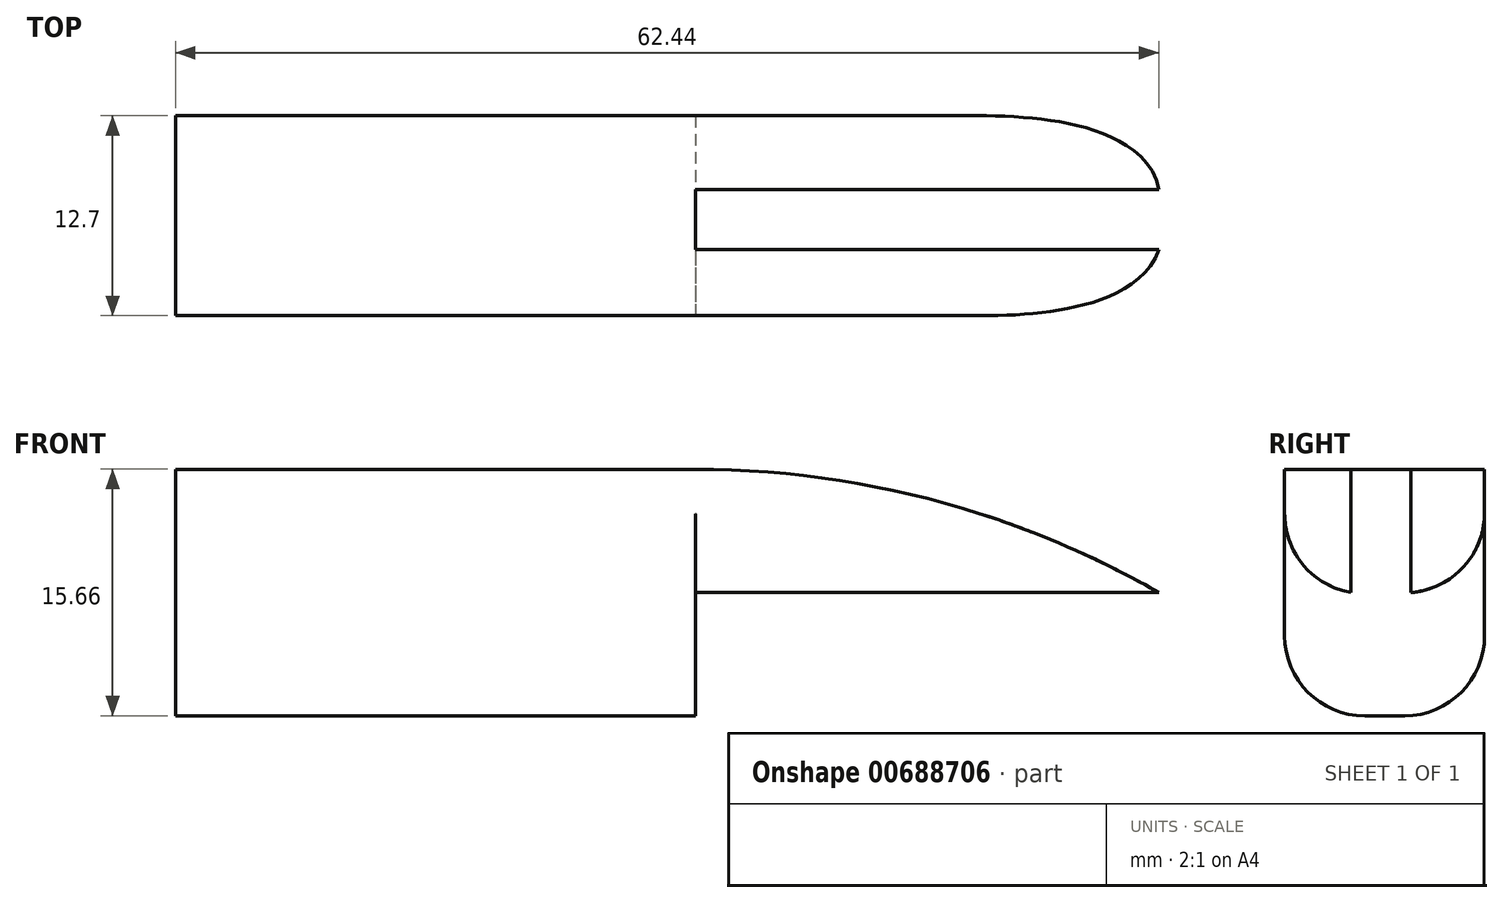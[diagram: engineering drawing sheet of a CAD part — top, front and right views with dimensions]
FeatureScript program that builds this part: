
annotation { "Feature Type Name" : "Feature", "Feature Type Description" : "" }
export const myFeature = defineFeature(function(context is Context, id is Id, definition is map)
    precondition{}
    {
        {
            var Q0;
            Q0=qCreatedBy(makeId("Front.planeOp"),FACE);
            var sketch = newSketch(context, id + "F0", { "sketchPlane" : qUnion([Q0])});
            skLineSegment(sketch, "E0", {"start": v(-26.64, 18.05) * mm, "end": v(6.38, 18.05) * mm});
            skLineSegment(sketch, "E1", {"start": v(-26.64, 2.39) * mm, "end": v(6.38, 2.39) * mm});
            skLineSegment(sketch, "E2", {"start": v(6.38, 2.39) * mm, "end": v(6.38, 18.05) * mm});
            skArc(sketch, "E3", {"start": v(35.8, 10.22) * mm, "mid": v(21.6, 16.05) * mm, "end": v(6.38, 18.05) * mm});
            skPoint(sketch, "E3.startSnap0", {"position": v(6.38, 10.22) * mm});
            skLineSegment(sketch, "E4", {"start": v(6.38, 10.22) * mm, "end": v(35.8, 10.22) * mm});
            skLineSegment(sketch, "E5", {"start": v(-26.64, 18.05) * mm, "end": v(-26.64, 2.39) * mm});
            skSolve(sketch);
        }
        {
            var Q0;
            Q0 = qSketchRegion(id + "F0", true);
            extrude(context, id + "F1", {"entities" : qUnion([Q0]), "depth" : 12.7 * mm, "offsetDistance" : 25.4 * mm});
        }
        {
            var Q0;
            Q0=makeQuery(id+"F1.opExtrude","SWEPT_FACE",FACE,{"disambiguationData":[OSD([sQuery(id+"F0.wireOp",EDGE,"E4")])]});
            var sketch = newSketch(context, id + "F2", { "sketchPlane" : qUnion([Q0])});
            skLineSegment(sketch, "E6", {"start": v(6.38, 4.68) * mm, "end": v(35.8, 4.68) * mm});
            skLineSegment(sketch, "E7", {"start": v(35.8, 4.68) * mm, "end": v(35.8, 8.5) * mm});
            skLineSegment(sketch, "E8", {"start": v(35.8, 8.5) * mm, "end": v(6.38, 8.5) * mm});
            skLineSegment(sketch, "E9", {"start": v(6.38, 8.5) * mm, "end": v(6.38, 4.68) * mm});
            skSolve(sketch);
        }
        {
            var Q0;
            Q0=makeQuery(id+"F2.imprint","IMPRINT",FACE,{"disambiguationData":[TD([[makeQuery(id+"F2.imprint","IMPRINT",EDGE,{"derivedFrom":sQuery(id+"F2.wireOp",EDGE,"E6")}),1.0]])]});
            extrude(context, id + "F3", {"entities" : qUnion([Q0]), "operationType" : NewBodyOperationType.REMOVE, "oppositeDirection" : true, "depth" : 25.4 * mm, "offsetDistance" : 25.4 * mm});
        }
        {
            var Q0;
            Q0=makeQuery(id+"F1.opExtrude","CAP_EDGE",EDGE,{"disambiguationData":[OSD([sQuery(id+"F0.wireOp",EDGE,"E1")])],"isStart":false});
            var Q1;
            Q1=makeQuery(id+"F1.opExtrude","CAP_EDGE",EDGE,{"disambiguationData":[OSD([sQuery(id+"F0.wireOp",EDGE,"E1")])],"isStart":true});
            var Q2;
            Q2=makeQuery(id+"F1.opExtrude","CAP_EDGE",EDGE,{"disambiguationData":[OSD([sQuery(id+"F0.wireOp",EDGE,"E4")])],"isStart":false});
            var Q3;
            Q3=makeQuery(id+"F1.opExtrude","CAP_EDGE",EDGE,{"disambiguationData":[OSD([sQuery(id+"F0.wireOp",EDGE,"E4")])],"isStart":true});
            fillet(context, id + "F4", {"entities" : qUnion([Q0, Q1, Q2, Q3]), "radius" : 5.08 * mm, "tangentPropagation" : true, "allowEdgeOverflow" : false});
        }
    });
